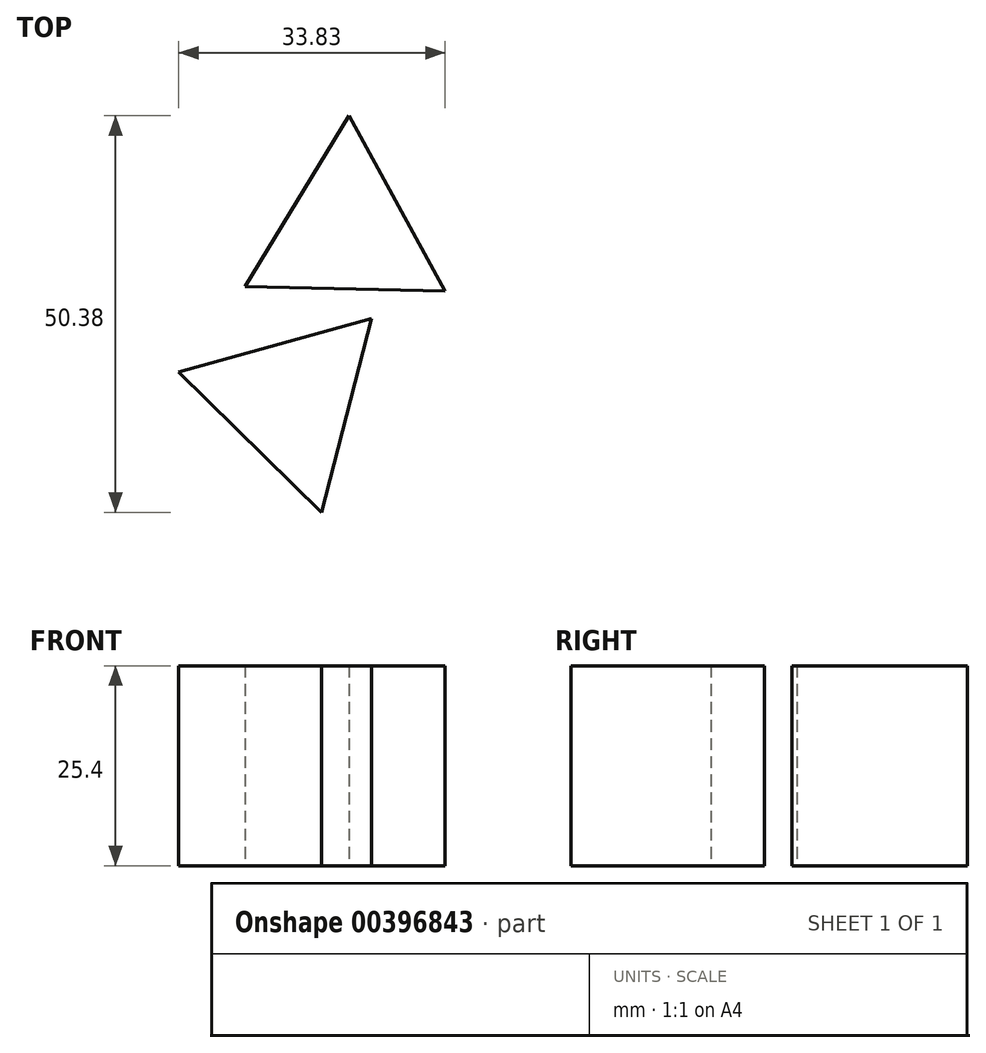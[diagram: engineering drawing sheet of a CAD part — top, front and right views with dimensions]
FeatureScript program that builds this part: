
annotation { "Feature Type Name" : "Feature", "Feature Type Description" : "" }
export const myFeature = defineFeature(function(context is Context, id is Id, definition is map)
    precondition{}
    {
        {
            var Q0;
            Q0=qCreatedBy(makeId("Top.planeOp"),FACE);
            var sketch = newSketch(context, id + "F0", { "sketchPlane" : qUnion([Q0])});
            skCircle(sketch, "E0.cCircle", {"center": v(0, 21.59) * mm, "radius": 7.33 * mm, "construction": true});
            skLineSegment(sketch, "E0.0", {"start": v(12.53, 13.96) * mm, "end": v(-12.87, 14.55) * mm});
            skLineSegment(sketch, "E0.1", {"start": v(-12.87, 14.55) * mm, "end": v(0.34, 36.25) * mm});
            skLineSegment(sketch, "E0.2", {"start": v(0.34, 36.25) * mm, "end": v(12.53, 13.96) * mm});
            skPoint(sketch, "E0.0.midPoint", {"position": v(-0.17, 14.26) * mm});
            skSolve(sketch);
        }
        {
            var Q0;
            Q0=makeQuery(id+"F0.imprint","IMPRINT",FACE,{"disambiguationData":[TD([[makeQuery(id+"F0.imprint","IMPRINT",EDGE,{"derivedFrom":sQuery(id+"F0.wireOp",EDGE,"E0.0")}),-1.0]])]});
            extrude(context, id + "F1", {"entities" : qUnion([Q0]), "depth" : 25.4 * mm});
        }
        {
            var Q0;
            Q0=qCreatedBy(makeId("Top.planeOp"),FACE);
            var sketch = newSketch(context, id + "F2", { "sketchPlane" : qUnion([Q0])});
            skCircle(sketch, "E1.cCircle", {"center": v(-7.1, 0) * mm, "radius": 7.33 * mm, "construction": true});
            skLineSegment(sketch, "E1.0", {"start": v(3.17, 10.46) * mm, "end": v(-3.17, -14.13) * mm});
            skLineSegment(sketch, "E1.1", {"start": v(-3.17, -14.13) * mm, "end": v(-21.3, 3.67) * mm});
            skLineSegment(sketch, "E1.2", {"start": v(-21.3, 3.67) * mm, "end": v(3.17, 10.46) * mm});
            skPoint(sketch, "E1.0.midPoint", {"position": v(0, -1.83) * mm});
            skSolve(sketch);
        }
        {
            var Q0;
            Q0=makeQuery(id+"F2.imprint","IMPRINT",FACE,{"disambiguationData":[TD([[makeQuery(id+"F2.imprint","IMPRINT",EDGE,{"derivedFrom":sQuery(id+"F2.wireOp",EDGE,"E1.0")}),-1.0]])]});
            extrude(context, id + "F3", {"entities" : qUnion([Q0]), "depth" : 25.4 * mm});
        }
    });
